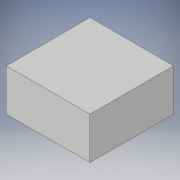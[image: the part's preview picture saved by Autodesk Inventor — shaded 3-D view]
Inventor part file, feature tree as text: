
AUTODESK INVENTOR PART (.ipt)
format: ipt  version: 2019.3 (Build 233278000, 278)  size: 87,040 bytes
history: native  units: mm
features: other x1, extrude x1, sketch x1
ambient origin geometry x8: Origin, YZ Plane, XZ Plane, XY Plane, X Axis, Y Axis, Z Axis, Center Point
bodies: Body1 (feature_tree)
feature tree (3):
  other  "ソリッド1"
  extrude  "押し出し1"  Depth=50.0mm
  sketch  "スケッチ1"
